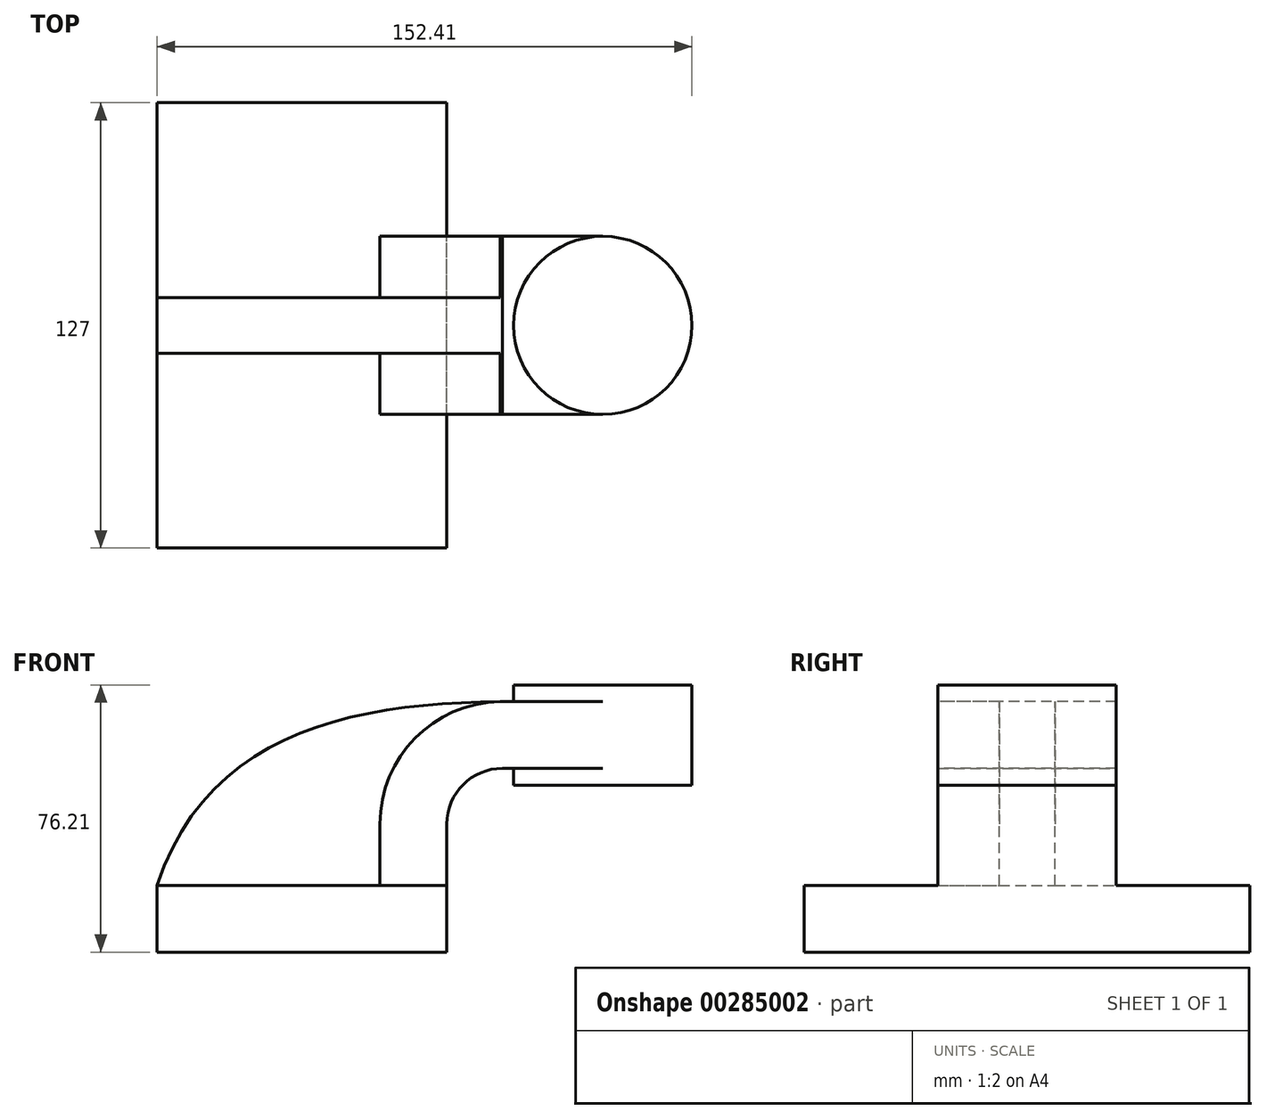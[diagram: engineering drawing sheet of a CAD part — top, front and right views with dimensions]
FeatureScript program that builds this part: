
annotation { "Feature Type Name" : "Feature", "Feature Type Description" : "" }
export const myFeature = defineFeature(function(context is Context, id is Id, definition is map)
    precondition{}
    {
        {
            var Q0;
            Q0=qCreatedBy(makeId("Front.planeOp"),FACE);
            var sketch = newSketch(context, id + "F0", { "sketchPlane" : qUnion([Q0])});
            skLineSegment(sketch, "E0.bottom", {"start": v(41.28, -9.52) * mm, "end": v(-41.28, -9.53) * mm});
            skLineSegment(sketch, "E0.top", {"start": v(41.28, 9.53) * mm, "end": v(-41.28, 9.53) * mm});
            skLineSegment(sketch, "E0.left", {"start": v(41.28, -9.52) * mm, "end": v(41.28, 9.53) * mm});
            skLineSegment(sketch, "E0.right", {"start": v(-41.28, -9.53) * mm, "end": v(-41.28, 9.53) * mm});
            skPoint(sketch, "E0.middle", {"position": v(0, 0) * mm});
            skLineSegment(sketch, "E1.bottom", {"start": v(111.12, 38.1) * mm, "end": v(60.32, 38.1) * mm});
            skLineSegment(sketch, "E1.top", {"start": v(111.12, 66.68) * mm, "end": v(60.32, 66.68) * mm});
            skLineSegment(sketch, "E1.left", {"start": v(111.12, 38.1) * mm, "end": v(111.12, 66.68) * mm});
            skLineSegment(sketch, "E1.right", {"start": v(60.32, 38.1) * mm, "end": v(60.32, 66.67) * mm});
            skPoint(sketch, "E1.middle", {"position": v(85.72, 52.39) * mm});
            skLineSegment(sketch, "E2", {"start": v(41.28, 9.53) * mm, "end": v(41.28, 27) * mm});
            skArc(sketch, "E3", {"start": v(41.27, 27) * mm, "mid": v(45.92, 38.23) * mm, "end": v(57.15, 42.88) * mm});
            skLineSegment(sketch, "E4", {"start": v(57.15, 42.88) * mm, "end": v(85.73, 42.88) * mm});
            skArc(sketch, "E5.0", {"start": v(22.23, 27) * mm, "mid": v(32.45, 51.7) * mm, "end": v(57.15, 61.93) * mm});
            skLineSegment(sketch, "E6.0", {"start": v(22.22, 9.53) * mm, "end": v(22.22, 27) * mm});
            skLineSegment(sketch, "E7.0", {"start": v(57.15, 61.93) * mm, "end": v(85.73, 61.93) * mm});
            skLineSegment(sketch, "E8", {"start": v(85.72, 66.68) * mm, "end": v(85.72, 38.1) * mm});
            skFitSpline(sketch, "E9", {"points": [v(-41.28, 9.53) * mm, v(57.15, 61.93) * mm], "startDerivative": vector(43.56, 131.65) * mm, "endDerivative": vector(127.72, 1.18) * mm});
            skSolve(sketch);
        }
        {
            var Q0;
            Q0=makeQuery(id+"F0.imprint","IMPRINT",FACE,{"disambiguationData":[TD([[makeQuery(id+"F0.imprint","IMPRINT",EDGE,{"derivedFrom":sQuery(id+"F0.wireOp",EDGE,"E0.bottom")}),-1.0]])]});
            extrude(context, id + "F1", {"entities" : qUnion([Q0]), "depth" : 127 * mm, "symmetric" : true});
        }
        {
            var Q0;
            {var subQ1=sQuery(id+"F0.wireOp",EDGE,"E2");Q0=makeQuery(id+"F0.imprint","IMPRINT",FACE,{"disambiguationData":[TD([[makeQuery(id+"F0.imprint","IMPRINT",EDGE,{"derivedFrom":subQ1}),1.0]])]});}
            var Q1;
            {var subQ0=sQuery(id+"F0.wireOp",EDGE,"E4");var subQ1=sQuery(id+"F0.wireOp",EDGE,"E1.right");var subQ2=makeQuery(id+"F0.imprint","INTERSECT",VERTEX,{"derivedFrom":[subQ1,subQ0]});Q1=makeQuery(id+"F0.imprint","IMPRINT",FACE,{"disambiguationData":[TD([[makeQuery(id+"F0.imprint","IMPRINT",EDGE,{"disambiguationData":[TD([[subQ2,-1.0]])],"derivedFrom":subQ1}),-1.0]])]});}
            extrude(context, id + "F2", {"entities" : qUnion([Q0, Q1]), "operationType" : NewBodyOperationType.ADD, "depth" : 50.8 * mm, "symmetric" : true});
        }
        {
            var Q0;
            {var subQ3=sQuery(id+"F0.wireOp",EDGE,"E6.0");Q0=makeQuery(id+"F0.imprint","IMPRINT",FACE,{"disambiguationData":[TD([[makeQuery(id+"F0.imprint","IMPRINT",EDGE,{"derivedFrom":subQ3}),1.0]])]});}
            extrude(context, id + "F3", {"entities" : qUnion([Q0]), "operationType" : NewBodyOperationType.ADD, "depth" : 15.88 * mm, "symmetric" : true});
        }
        {
            var Q0;
            {var subQ0=sQuery(id+"F0.wireOp",EDGE,"E1.left");Q0=makeQuery(id+"F0.imprint","IMPRINT",FACE,{"disambiguationData":[TD([[makeQuery(id+"F0.imprint","IMPRINT",EDGE,{"derivedFrom":subQ0}),1.0]])]});}
            var Q1;
            Q1=sQuery(id+"F0.wireOp",EDGE,"E8");
            revolve(context, id + "F4", {"operationType" : NewBodyOperationType.ADD, "entities" : qUnion([Q0]), "axis" : qUnion([Q1]), "revolveType" : RevolveType.FULL});
        }
    });
